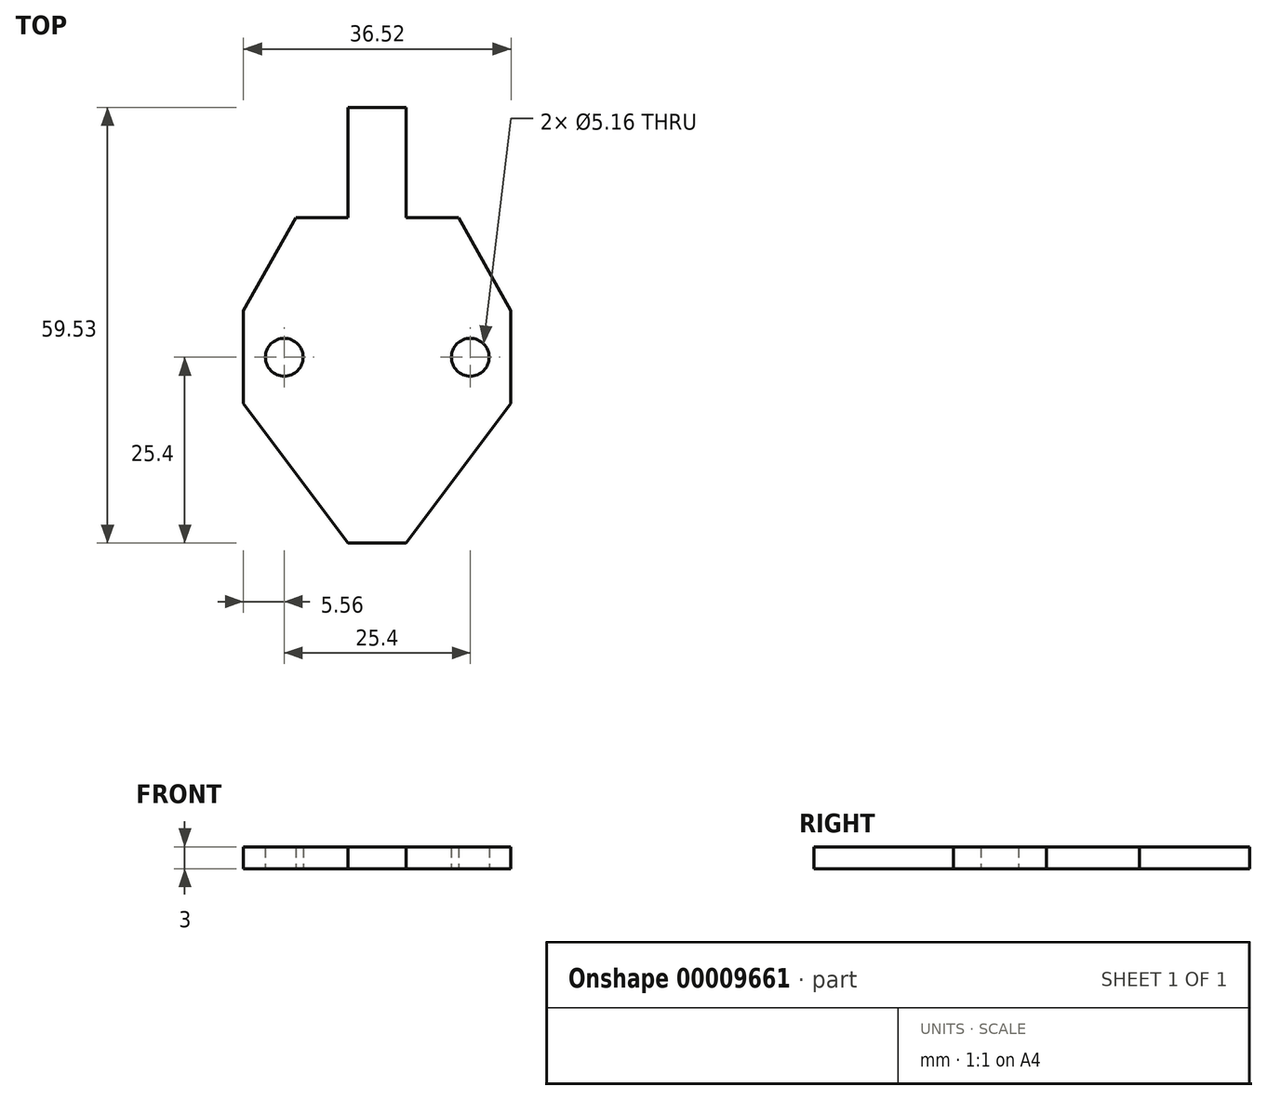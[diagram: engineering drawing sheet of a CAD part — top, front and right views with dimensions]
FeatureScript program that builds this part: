
annotation { "Feature Type Name" : "Feature", "Feature Type Description" : "" }
export const myFeature = defineFeature(function(context is Context, id is Id, definition is map)
    precondition{}
    {
        {
            var Q0;
            Q0=qCreatedBy(makeId("Top.planeOp"),FACE);
            var sketch = newSketch(context, id + "F0", { "sketchPlane" : qUnion([Q0])});
            skLineSegment(sketch, "E0", {"start": v(0, 0) * mm, "end": v(0, 15.08) * mm, "construction": true});
            skLineSegment(sketch, "E1", {"start": v(0, 15.08) * mm, "end": v(-3.97, 15.08) * mm});
            skLineSegment(sketch, "E2", {"start": v(-3.97, 15.08) * mm, "end": v(-3.97, 0) * mm});
            skLineSegment(sketch, "E3", {"start": v(-3.97, 0) * mm, "end": v(-11.11, 0) * mm});
            skLineSegment(sketch, "E4", {"start": v(-11.11, 0) * mm, "end": v(-18.26, -12.7) * mm});
            skLineSegment(sketch, "E5", {"start": v(-18.26, -12.7) * mm, "end": v(-18.26, -25.4) * mm});
            skLineSegment(sketch, "E6", {"start": v(-18.26, -25.4) * mm, "end": v(-3.97, -44.45) * mm});
            skLineSegment(sketch, "E7", {"start": v(-3.97, -44.45) * mm, "end": v(0, -44.45) * mm});
            skCircle(sketch, "E8", {"center": v(-12.7, -19.05) * mm, "radius": 2.58 * mm});
            skLineSegment(sketch, "E9.0.MirrorCS", {"start": v(0, 15.08) * mm, "end": v(3.97, 15.08) * mm});
            skLineSegment(sketch, "E10.0.MirrorCS", {"start": v(3.97, 15.08) * mm, "end": v(3.97, 0) * mm});
            skLineSegment(sketch, "E11.0.MirrorCS", {"start": v(3.97, 0) * mm, "end": v(11.11, 0) * mm});
            skLineSegment(sketch, "E12.0.MirrorCS", {"start": v(11.11, 0) * mm, "end": v(18.26, -12.7) * mm});
            skLineSegment(sketch, "E13.0.MirrorCS", {"start": v(18.26, -12.7) * mm, "end": v(18.26, -25.4) * mm});
            skCircle(sketch, "E14.0.MirrorC", {"center": v(12.7, -19.05) * mm, "radius": 2.58 * mm});
            skLineSegment(sketch, "E15.0.MirrorCS", {"start": v(18.26, -25.4) * mm, "end": v(3.97, -44.45) * mm});
            skLineSegment(sketch, "E16.0.MirrorCS", {"start": v(3.97, -44.45) * mm, "end": v(0, -44.45) * mm});
            skSolve(sketch);
        }
        {
            var Q0;
            Q0=makeQuery(id+"F0.imprint","IMPRINT",FACE,{"disambiguationData":[TD([[makeQuery(id+"F0.imprint","IMPRINT",EDGE,{"derivedFrom":sQuery(id+"F0.wireOp",EDGE,"E1")}),1.0]])]});
            extrude(context, id + "F1", {"entities" : qUnion([Q0]), "depth" : 3 * mm});
        }
    });
